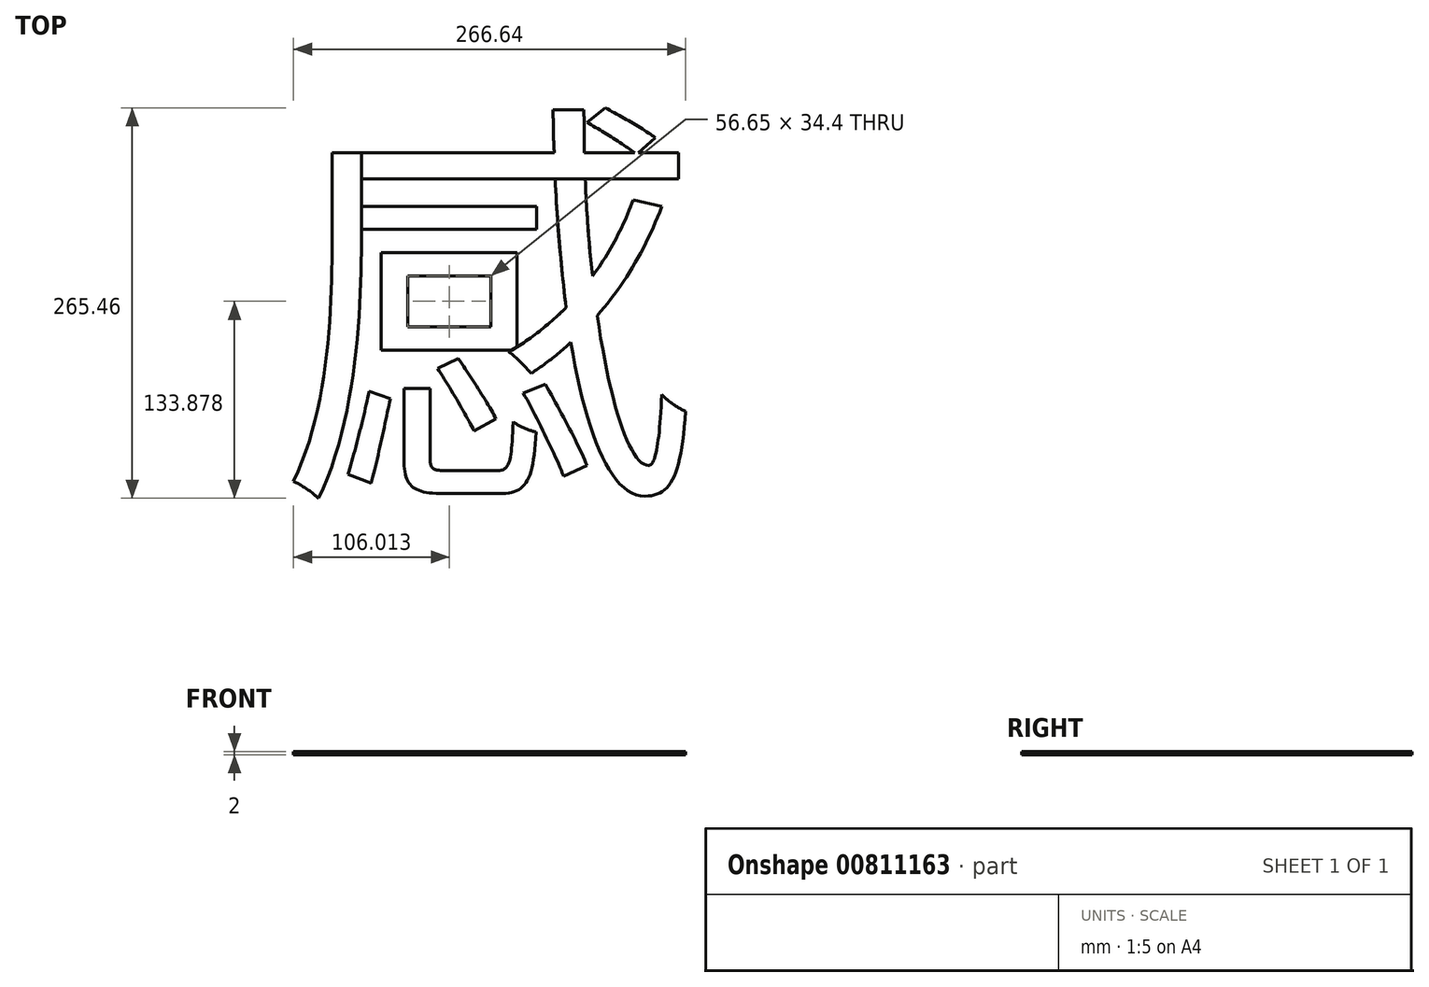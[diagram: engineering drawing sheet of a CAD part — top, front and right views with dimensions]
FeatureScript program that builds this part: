
annotation { "Feature Type Name" : "Feature", "Feature Type Description" : "" }
export const myFeature = defineFeature(function(context is Context, id is Id, definition is map)
    precondition{}
    {
        {
            var Q0;
            Q0=qCreatedBy(makeId("Top.planeOp"),FACE);
            var sketch = newSketch(context, id + "F0", { "sketchPlane" : qUnion([Q0])});
            skText(sketch, "E0", { "text": "感", "fontName": "NotoSansCJKtc-Regular.otf"});
            const initialGuessF0  = {"E0": [0, 0, 1, 0, 0.208]};
            skSetInitialGuess(sketch, initialGuessF0);
            skSolve(sketch);
        }
        {
            var Q0;
            Q0 = qSketchRegion(id + "F0", true);
            extrude(context, id + "F1", {"entities" : qUnion([Q0]), "depth" : 2 * mm, "offsetDistance" : 25.4 * mm});
        }
        {
            var Q0;
            Q0=makeQuery(id+"F1.opExtrude","CAP_FACE",FACE,{"disambiguationData":[OSD([sQuery(id+"F0.wireOp",EDGE,"E0.sketch_text.stroke-22"),sQuery(id+"F0.wireOp",EDGE,"E0.sketch_text.stroke-23"),sQuery(id+"F0.wireOp",EDGE,"E0.sketch_text.stroke-24"),sQuery(id+"F0.wireOp",EDGE,"E0.sketch_text.stroke-25"),sQuery(id+"F0.wireOp",EDGE,"E0.sketch_text.stroke-26"),sQuery(id+"F0.wireOp",EDGE,"E0.sketch_text.stroke-27"),sQuery(id+"F0.wireOp",EDGE,"E0.sketch_text.stroke-28"),sQuery(id+"F0.wireOp",EDGE,"E0.sketch_text.stroke-29"),sQuery(id+"F0.wireOp",EDGE,"E0.sketch_text.stroke-30"),sQuery(id+"F0.wireOp",EDGE,"E0.sketch_text.stroke-31"),sQuery(id+"F0.wireOp",EDGE,"E0.sketch_text.stroke-32"),sQuery(id+"F0.wireOp",EDGE,"E0.sketch_text.stroke-33"),sQuery(id+"F0.wireOp",EDGE,"E0.sketch_text.stroke-34"),sQuery(id+"F0.wireOp",EDGE,"E0.sketch_text.stroke-35"),sQuery(id+"F0.wireOp",EDGE,"E0.sketch_text.stroke-36"),sQuery(id+"F0.wireOp",EDGE,"E0.sketch_text.stroke-37"),sQuery(id+"F0.wireOp",EDGE,"E0.sketch_text.stroke-38"),sQuery(id+"F0.wireOp",EDGE,"E0.sketch_text.stroke-39"),sQuery(id+"F0.wireOp",EDGE,"E0.sketch_text.stroke-40"),sQuery(id+"F0.wireOp",EDGE,"E0.sketch_text.stroke-41"),sQuery(id+"F0.wireOp",EDGE,"E0.sketch_text.stroke-42"),sQuery(id+"F0.wireOp",EDGE,"E0.sketch_text.stroke-43"),sQuery(id+"F0.wireOp",EDGE,"E0.sketch_text.stroke-44"),sQuery(id+"F0.wireOp",EDGE,"E0.sketch_text.stroke-45"),sQuery(id+"F0.wireOp",EDGE,"E0.sketch_text.stroke-46"),sQuery(id+"F0.wireOp",EDGE,"E0.sketch_text.stroke-47"),sQuery(id+"F0.wireOp",EDGE,"E0.sketch_text.stroke-48"),sQuery(id+"F0.wireOp",EDGE,"E0.sketch_text.stroke-49"),sQuery(id+"F0.wireOp",EDGE,"E0.sketch_text.stroke-50"),sQuery(id+"F0.wireOp",EDGE,"E0.sketch_text.stroke-51"),sQuery(id+"F0.wireOp",EDGE,"E0.sketch_text.stroke-52"),sQuery(id+"F0.wireOp",EDGE,"E0.sketch_text.stroke-53"),sQuery(id+"F0.wireOp",EDGE,"E0.sketch_text.stroke-54"),sQuery(id+"F0.wireOp",EDGE,"E0.sketch_text.stroke-55"),sQuery(id+"F0.wireOp",EDGE,"E0.sketch_text.stroke-56"),sQuery(id+"F0.wireOp",EDGE,"E0.sketch_text.stroke-57"),sQuery(id+"F0.wireOp",EDGE,"E0.sketch_text.stroke-58"),sQuery(id+"F0.wireOp",EDGE,"E0.sketch_text.stroke-59"),sQuery(id+"F0.wireOp",EDGE,"E0.sketch_text.stroke-60"),sQuery(id+"F0.wireOp",EDGE,"E0.sketch_text.stroke-61"),sQuery(id+"F0.wireOp",EDGE,"E0.sketch_text.stroke-62"),sQuery(id+"F0.wireOp",EDGE,"E0.sketch_text.stroke-63"),sQuery(id+"F0.wireOp",EDGE,"E0.sketch_text.stroke-64"),sQuery(id+"F0.wireOp",EDGE,"E0.sketch_text.stroke-65")])],"isStart":false});
            var sketch = newSketch(context, id + "F2", { "sketchPlane" : qUnion([Q0])});
            skLineSegment(sketch, "E1.bottom", {"start": v(57.5, 160.33) * mm, "end": v(57.6, 160.33) * mm});
            skLineSegment(sketch, "E1.top", {"start": v(57.5, 212.6) * mm, "end": v(57.6, 212.6) * mm});
            skLineSegment(sketch, "E1.left", {"start": v(57.5, 160.33) * mm, "end": v(57.5, 212.6) * mm});
            skLineSegment(sketch, "E1.right", {"start": v(57.6, 160.33) * mm, "end": v(57.6, 212.6) * mm});
            skLineSegment(sketch, "E2.bottom", {"start": v(189.22, 194.73) * mm, "end": v(209.72, 194.73) * mm});
            skLineSegment(sketch, "E2.top", {"start": v(189.22, 194.63) * mm, "end": v(209.72, 194.63) * mm});
            skLineSegment(sketch, "E2.left", {"start": v(189.22, 194.73) * mm, "end": v(189.22, 194.63) * mm});
            skLineSegment(sketch, "E2.right", {"start": v(209.72, 194.73) * mm, "end": v(209.72, 194.63) * mm});
            skSolve(sketch);
        }
        {
            var Q0;
            Q0 = qSketchRegion(id + "F2", true);
            extrude(context, id + "F3", {"entities" : qUnion([Q0]), "operationType" : NewBodyOperationType.REMOVE, "oppositeDirection" : true, "depth" : 25.4 * mm, "offsetDistance" : 25.4 * mm});
        }
        {
            var Q0;
            {var subQ0=sQuery(id+"F0.wireOp",EDGE,"E0.sketch_text.stroke-65");var subQ1=sQuery(id+"F0.wireOp",EDGE,"E0.sketch_text.stroke-64");var subQ2=sQuery(id+"F0.wireOp",EDGE,"E0.sketch_text.stroke-63");var subQ3=sQuery(id+"F0.wireOp",EDGE,"E0.sketch_text.stroke-62");var subQ4=sQuery(id+"F0.wireOp",EDGE,"E0.sketch_text.stroke-61");var subQ5=sQuery(id+"F0.wireOp",EDGE,"E0.sketch_text.stroke-60");var subQ6=sQuery(id+"F0.wireOp",EDGE,"E0.sketch_text.stroke-59");var subQ7=sQuery(id+"F0.wireOp",EDGE,"E0.sketch_text.stroke-58");var subQ8=sQuery(id+"F0.wireOp",EDGE,"E0.sketch_text.stroke-57");var subQ9=sQuery(id+"F0.wireOp",EDGE,"E0.sketch_text.stroke-56");var subQ10=sQuery(id+"F0.wireOp",EDGE,"E0.sketch_text.stroke-55");var subQ11=sQuery(id+"F0.wireOp",EDGE,"E0.sketch_text.stroke-54");var subQ12=sQuery(id+"F0.wireOp",EDGE,"E0.sketch_text.stroke-24");var subQ13=sQuery(id+"F0.wireOp",EDGE,"E0.sketch_text.stroke-23");var subQ14=sQuery(id+"F0.wireOp",EDGE,"E0.sketch_text.stroke-25");var subQ15=sQuery(id+"F0.wireOp",EDGE,"E0.sketch_text.stroke-22");var subQ16=sQuery(id+"F0.wireOp",EDGE,"E0.sketch_text.stroke-53");var subQ17=sQuery(id+"F0.wireOp",EDGE,"E0.sketch_text.stroke-26");var subQ18=sQuery(id+"F0.wireOp",EDGE,"E0.sketch_text.stroke-27");var subQ19=sQuery(id+"F0.wireOp",EDGE,"E0.sketch_text.stroke-50");var subQ20=sQuery(id+"F0.wireOp",EDGE,"E0.sketch_text.stroke-51");var subQ21=sQuery(id+"F0.wireOp",EDGE,"E0.sketch_text.stroke-52");Q0=makeQuery(id+"F3.boolean.opBoolean","SPLIT",FACE,{"disambiguationData":[TD([makeQuery(id+"F1.opExtrude","SWEPT_FACE",FACE,{"disambiguationData":[OSD([subQ15])]})])],"derivedFrom":makeQuery(id+"F1.opExtrude","CAP_FACE",FACE,{"disambiguationData":[OSD([subQ15,subQ13,subQ12,subQ14,subQ17,subQ18,sQuery(id+"F0.wireOp",EDGE,"E0.sketch_text.stroke-28"),sQuery(id+"F0.wireOp",EDGE,"E0.sketch_text.stroke-29"),sQuery(id+"F0.wireOp",EDGE,"E0.sketch_text.stroke-30"),sQuery(id+"F0.wireOp",EDGE,"E0.sketch_text.stroke-31"),sQuery(id+"F0.wireOp",EDGE,"E0.sketch_text.stroke-32"),sQuery(id+"F0.wireOp",EDGE,"E0.sketch_text.stroke-33"),sQuery(id+"F0.wireOp",EDGE,"E0.sketch_text.stroke-34"),sQuery(id+"F0.wireOp",EDGE,"E0.sketch_text.stroke-35"),sQuery(id+"F0.wireOp",EDGE,"E0.sketch_text.stroke-36"),sQuery(id+"F0.wireOp",EDGE,"E0.sketch_text.stroke-37"),sQuery(id+"F0.wireOp",EDGE,"E0.sketch_text.stroke-38"),sQuery(id+"F0.wireOp",EDGE,"E0.sketch_text.stroke-39"),sQuery(id+"F0.wireOp",EDGE,"E0.sketch_text.stroke-40"),sQuery(id+"F0.wireOp",EDGE,"E0.sketch_text.stroke-41"),sQuery(id+"F0.wireOp",EDGE,"E0.sketch_text.stroke-42"),sQuery(id+"F0.wireOp",EDGE,"E0.sketch_text.stroke-43"),sQuery(id+"F0.wireOp",EDGE,"E0.sketch_text.stroke-44"),sQuery(id+"F0.wireOp",EDGE,"E0.sketch_text.stroke-45"),sQuery(id+"F0.wireOp",EDGE,"E0.sketch_text.stroke-46"),sQuery(id+"F0.wireOp",EDGE,"E0.sketch_text.stroke-47"),sQuery(id+"F0.wireOp",EDGE,"E0.sketch_text.stroke-48"),sQuery(id+"F0.wireOp",EDGE,"E0.sketch_text.stroke-49"),subQ19,subQ20,subQ21,subQ16,subQ11,subQ10,subQ9,subQ8,subQ7,subQ6,subQ5,subQ4,subQ3,subQ2,subQ1,subQ0])],"isStart":false})});}
            var sketch = newSketch(context, id + "F4", { "sketchPlane" : qUnion([Q0])});
            skLineSegment(sketch, "E3", {"start": v(159.75, 78.27) * mm, "end": v(163.22, 80.3) * mm});
            skLineSegment(sketch, "E4", {"start": v(163.22, 80.3) * mm, "end": v(163.22, 80.42) * mm});
            skLineSegment(sketch, "E5", {"start": v(163.22, 80.42) * mm, "end": v(159.55, 78.27) * mm});
            skLineSegment(sketch, "E6", {"start": v(159.55, 78.27) * mm, "end": v(159.75, 78.27) * mm});
            skSolve(sketch);
        }
        {
            var Q0;
            Q0 = qSketchRegion(id + "F4", true);
            extrude(context, id + "F5", {"entities" : qUnion([Q0]), "operationType" : NewBodyOperationType.REMOVE, "oppositeDirection" : true, "depth" : 25.4 * mm, "offsetDistance" : 25.4 * mm});
        }
    });
